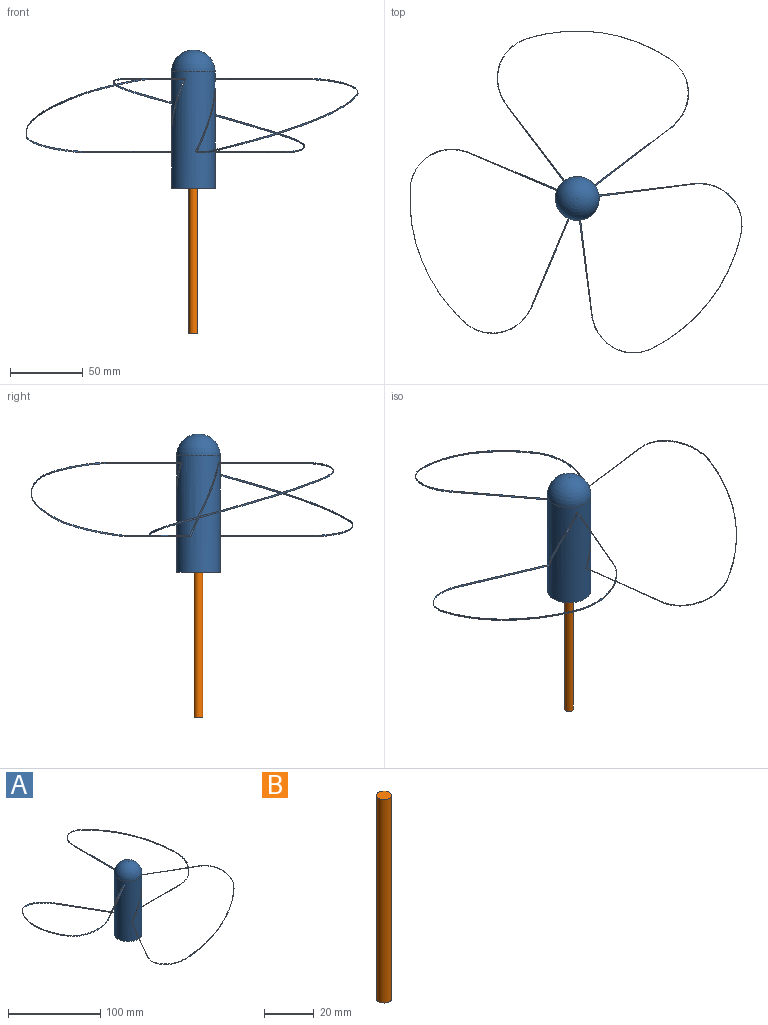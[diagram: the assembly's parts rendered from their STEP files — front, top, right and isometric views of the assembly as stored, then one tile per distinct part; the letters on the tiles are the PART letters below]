
ASSEMBLY  parts=2 mates=1
PART A: 20 faces, bbox 236.2x236.2x95 mm
  f0: cylinder r=15mm len=80mm, axis (0,0,-1), area 7374.1mm2, adj f1,f2,f3,f5,f11,f12,f13,f15
  f1: plane 30x30mm, normal (0,0,-1), area 678.6mm2, adj f0,f18
  f2: sphere r=15mm, area 1413.7mm2, adj f0
  f3: bspline ~56.97x33.26mm, area 65.3mm2, adj f0,f6
  f4: bspline ~101.74x31.17mm, area 107.2mm2, adj f6,f7
  f5: bspline ~72.47x42.19mm, area 65.3mm2, adj f0,f7
  f6: bspline ~43.55x38.43mm, area 56.9mm2, adj f3,f4
  f7: bspline ~47.87x35mm, area 56.9mm2, adj f4,f5
  f8: bspline ~41.14x39.5mm, area 56.9mm2, adj f9,f12
  f9: bspline ~74.48x74.48mm, area 107.2mm2, adj f8,f10
  f10: bspline ~41.14x39.5mm, area 56.9mm2, adj f9,f11
  f11: bspline ~83.33x0.95mm, area 65.3mm2, adj f0,f10
  f12: bspline ~65.42x0.93mm, area 65.3mm2, adj f0,f8
  f13: bspline ~56.97x33.26mm, area 65.3mm2, adj f0,f16
  f14: bspline ~101.74x31.17mm, area 107.2mm2, adj f16,f17
  f15: bspline ~72.47x42.19mm, area 65.3mm2, adj f0,f17
  f16: bspline ~47.87x35mm, area 56.9mm2, adj f13,f14
  f17: bspline ~43.55x38.43mm, area 56.9mm2, adj f14,f15
  f18: cylinder r=3mm len=50mm, axis (0,0,-1), area 942.5mm2, adj f1,f19
  f19: plane 6x6mm, normal (0,0,-1), area 28.3mm2, adj f18
PART B: 3 faces, bbox 6x6x100 mm
  f0: cylinder r=3mm len=100mm, axis (0,0,-1), area 1885mm2, adj f1,f2
  f1: plane 6x6mm, normal (0,0,1), area 28.3mm2, adj f0
  f2: plane 6x6mm, normal (0,0,-1), area 28.3mm2, adj f0
PLACE A rot(axis=(0,0,1),157.1deg) t=(23.33,-84.63,133.71)mm
PLACE B rot(axis=(0.75,0.66,0),180deg) t=(-14.14,-276.59,108.71)mm fixed
MATE revolute A.f18 <-> B.f0  axis (0,0,-1) through (23.33,-84.63,108.71)mm
